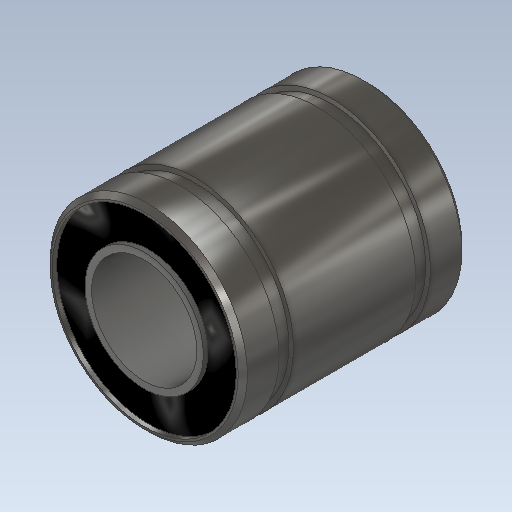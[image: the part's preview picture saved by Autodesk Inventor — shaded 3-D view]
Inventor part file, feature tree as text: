
AUTODESK INVENTOR PART (.ipt)
format: ipt  version: 2020 (Build 240168000, 168)  size: 242,176 bytes
history: native  units: mm
features: sketch x6, extrude x5, other x2, hole x1, chamfer x1
ambient origin geometry x8: Origin, YZ Plane, XZ Plane, XY Plane, X Axis, Y Axis, Z Axis, Center Point
bodies: Body1 (feature_tree)
feature tree (15):
  extrude  "Выдавливание2"  Depth=15.0mm
  hole  "Отверстие1"  [1 undecoded]
  other  "РабПлоскость1"
  other  "РабПлоскость2"
  sketch  "Эскиз10"
  extrude  "Выдавливание3"  [1 undecoded]
  extrude  "Выдавливание4"  [1 undecoded]
  extrude  "Выдавливание5"  Depth=14.3mm
  extrude  "Выдавливание6"  Depth=15.0mm
  chamfer  "Фаска1"  Distance=14.3mm
  sketch  "Эскиз6"
  sketch  "Эскиз8"
  sketch  "Эскиз11"
  sketch  "Эскиз12"
  sketch  "Эскиз13"
note: 3 required parameter values undecoded (feature->parameter linkage not recoverable at this tier; creation-order binding heuristic only, values carry confidence <= 0.55)
